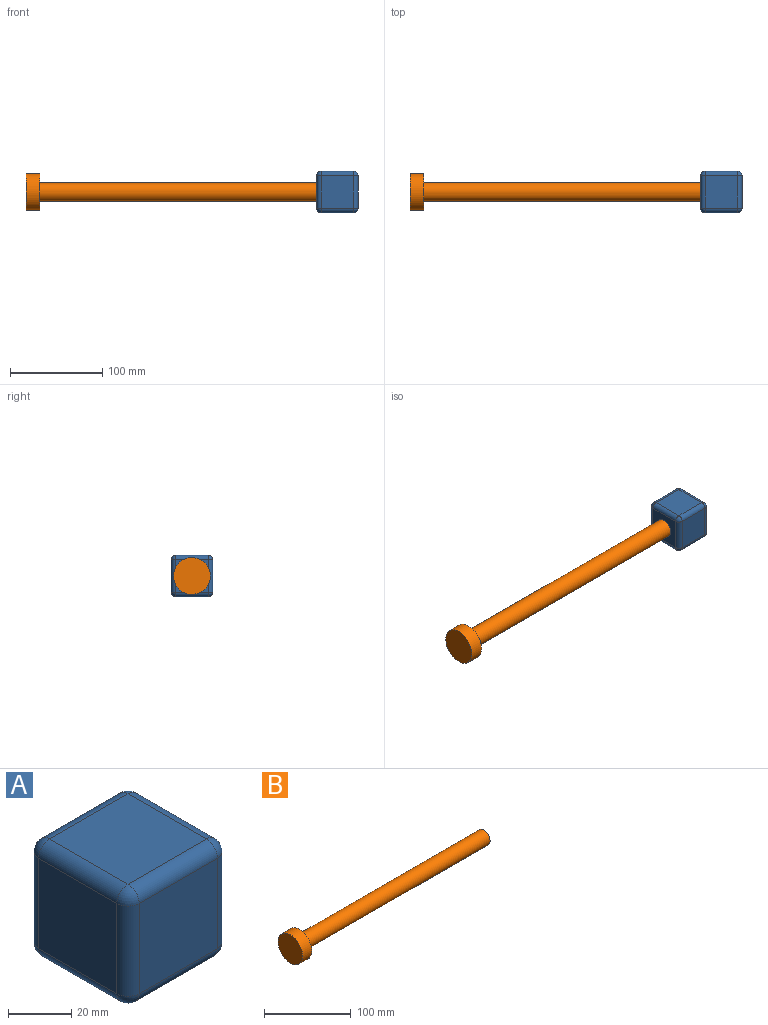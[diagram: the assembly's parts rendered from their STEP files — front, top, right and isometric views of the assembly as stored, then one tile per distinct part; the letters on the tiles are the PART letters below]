
ASSEMBLY  parts=2 mates=1
PART A: 26 faces, bbox 45x45x45 mm
  f0: plane 35x35mm, normal (1,0,0), area 1225mm2, adj f14,f19,f22,f25
  f1: plane 35x35mm, normal (0,0,1), area 1225mm2, adj f11,f20,f21,f25
  f2: plane 35x35mm, normal (-1,0,0), area 1225mm2, adj f6,f10,f11,f12
  f3: plane 35x35mm, normal (0,0,-1), area 1225mm2, adj f6,f9,f13,f14
  f4: plane 35x35mm, normal (0,-1,0), area 1225mm2, adj f9,f10,f19,f20
  f5: plane 35x35mm, normal (0,1,0), area 1225mm2, adj f12,f13,f21,f22
  f6: cylinder r=5mm len=35mm, axis (0,1,0), area 274.9mm2, adj f2,f3,f7,f8
  f7: sphere r=5mm, area 39.3mm2, adj f6,f9,f10
  f8: sphere r=5mm, area 39.3mm2, adj f6,f12,f13
  f9: cylinder r=5mm len=35mm, axis (-1,0,0), area 274.9mm2, adj f3,f4,f7,f15
  f10: cylinder r=5mm len=35mm, axis (0,0,1), area 274.9mm2, adj f2,f4,f7,f16
  f11: cylinder r=5mm len=35mm, axis (0,-1,0), area 274.9mm2, adj f1,f2,f16,f17
  f12: cylinder r=5mm len=35mm, axis (0,0,-1), area 274.9mm2, adj f2,f5,f8,f17
  f13: cylinder r=5mm len=35mm, axis (1,0,0), area 274.9mm2, adj f3,f5,f8,f18
  f14: cylinder r=5mm len=35mm, axis (0,-1,0), area 274.9mm2, adj f0,f3,f15,f18
  f15: sphere r=5mm, area 39.3mm2, adj f9,f14,f19
  f16: sphere r=5mm, area 39.3mm2, adj f10,f11,f20
  f17: sphere r=5mm, area 39.3mm2, adj f11,f12,f21
  f18: sphere r=5mm, area 39.3mm2, adj f13,f14,f22
  f19: cylinder r=5mm len=35mm, axis (0,0,-1), area 274.9mm2, adj f0,f4,f15,f23
  f20: cylinder r=5mm len=35mm, axis (1,0,0), area 274.9mm2, adj f1,f4,f16,f23
  f21: cylinder r=5mm len=35mm, axis (-1,0,0), area 274.9mm2, adj f1,f5,f17,f24
  f22: cylinder r=5mm len=35mm, axis (0,0,1), area 274.9mm2, adj f0,f5,f18,f24
  f23: sphere r=5mm, area 39.3mm2, adj f19,f20,f25
  f24: sphere r=5mm, area 39.3mm2, adj f21,f22,f25
  f25: cylinder r=5mm len=35mm, axis (0,1,0), area 274.9mm2, adj f0,f1,f23,f24
PART B: 5 faces, bbox 315x40x40 mm
  f0: cylinder r=10mm len=300mm, axis (-1,0,0), area 18849.6mm2, adj f1,f4
  f1: plane 20x20mm, normal (1,0,0), area 314.2mm2, adj f0
  f2: cylinder r=20mm len=40mm, axis (1,0,0), area 1885mm2, adj f3,f4
  f3: plane 40x40mm, normal (-1,0,0), area 1256.6mm2, adj f2
  f4: plane 40x40mm, normal (1,0,0), area 942.5mm2, adj f0,f2
PLACE A t=(191.1,46.46,-41.64)mm
PLACE B t=(-153.9,23.96,-19.14)mm
MATE fastened A.f2 <-> B.f0  axis (-1,0,0) through (146.1,23.96,-19.14)mm
